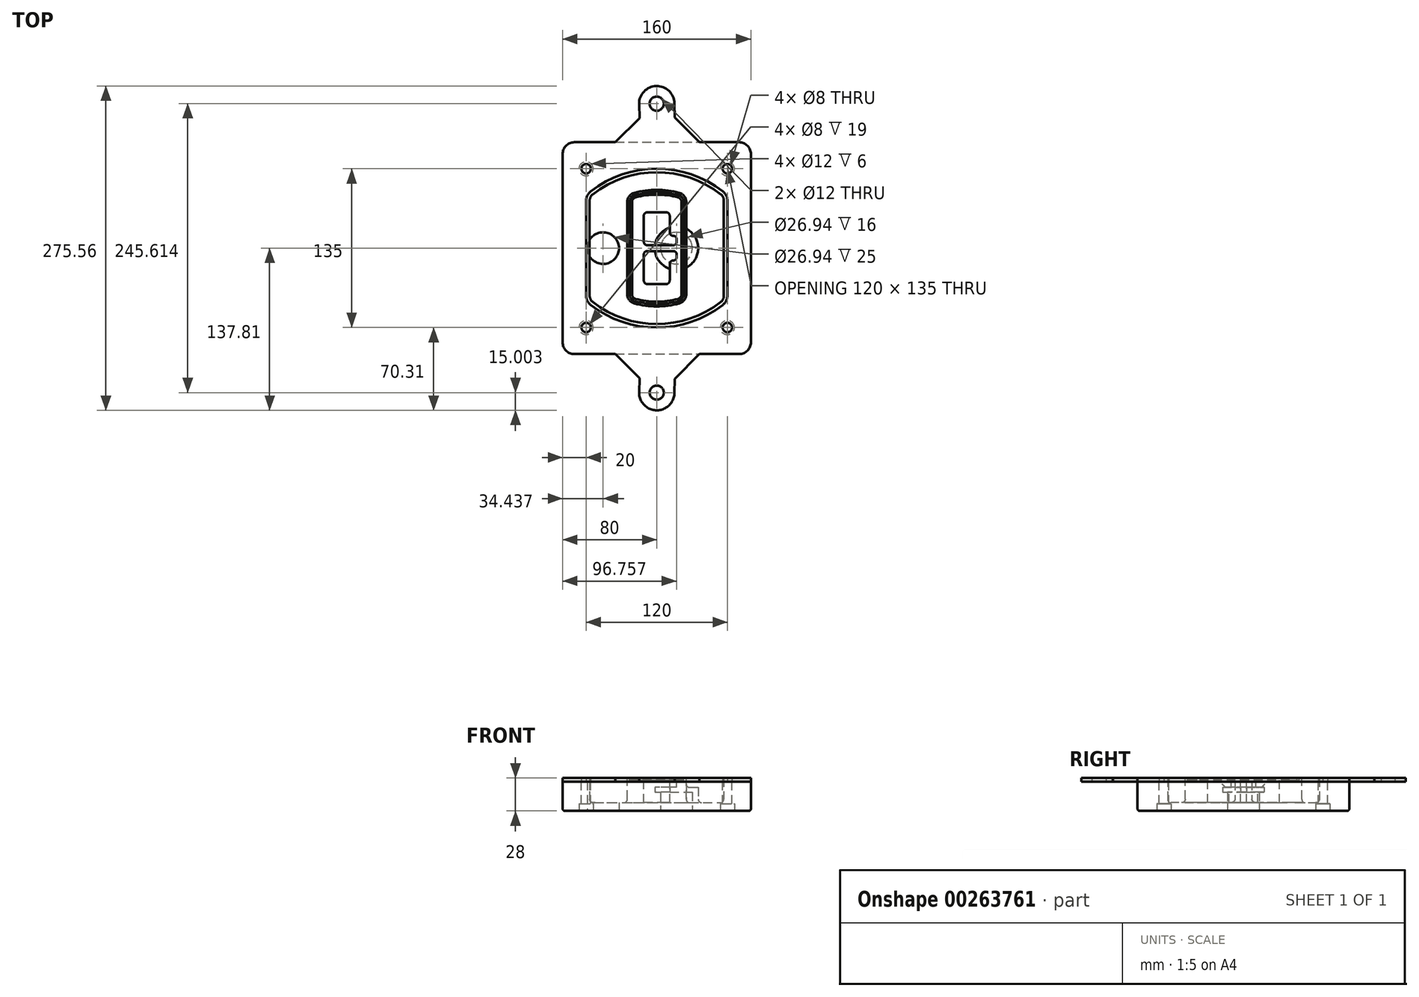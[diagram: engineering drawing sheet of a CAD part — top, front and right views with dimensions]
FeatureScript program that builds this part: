
annotation { "Feature Type Name" : "Feature", "Feature Type Description" : "" }
export const myFeature = defineFeature(function(context is Context, id is Id, definition is map)
    precondition{}
    {
        {
            var Q0;
            Q0=qCreatedBy(makeId("Top.planeOp"),FACE);
            var sketch = newSketch(context, id + "F0", { "sketchPlane" : qUnion([Q0])});
            skPoint(sketch, "E0.rect.middle", {"position": v(0, 0) * mm});
            skLineSegment(sketch, "E1.bottom", {"start": v(-70, -90) * mm, "end": v(70, -90) * mm});
            skLineSegment(sketch, "E1.top", {"start": v(-70, 90) * mm, "end": v(70, 90) * mm});
            skLineSegment(sketch, "E1.left", {"start": v(-80, -80) * mm, "end": v(-80, 80) * mm});
            skLineSegment(sketch, "E1.right", {"start": v(80, -80) * mm, "end": v(80, 80) * mm});
            skLineSegment(sketch, "E2", {"start": v(-80, 90) * mm, "end": v(80, -90) * mm, "construction": true});
            skLineSegment(sketch, "E3", {"start": v(80, 90) * mm, "end": v(-80, -90) * mm, "construction": true});
            skCircle(sketch, "E4", {"center": v(-60, 67.5) * mm, "radius": 4 * mm});
            skCircle(sketch, "E5", {"center": v(60, 67.5) * mm, "radius": 4 * mm});
            skCircle(sketch, "E6", {"center": v(60, -67.5) * mm, "radius": 4 * mm});
            skCircle(sketch, "E7", {"center": v(-60, -67.5) * mm, "radius": 4 * mm});
            skLineSegment(sketch, "E8", {"start": v(-60, 67.5) * mm, "end": v(60, 67.5) * mm, "construction": true});
            skLineSegment(sketch, "E9", {"start": v(60, 67.5) * mm, "end": v(60, -67.5) * mm, "construction": true});
            skLineSegment(sketch, "E10", {"start": v(60, -67.5) * mm, "end": v(-60, -67.5) * mm, "construction": true});
            skLineSegment(sketch, "E11", {"start": v(-60, -67.5) * mm, "end": v(-60, 67.5) * mm, "construction": true});
            skLineSegment(sketch, "E12", {"start": v(-60, 40.3) * mm, "end": v(-60, -40.3) * mm});
            skLineSegment(sketch, "E13", {"start": v(60, 40.3) * mm, "end": v(60, -40.3) * mm});
            skArc(sketch, "E14", {"start": v(56.15, 48.18) * mm, "mid": v(0, 67.5) * mm, "end": v(-56.15, 48.18) * mm});
            skArc(sketch, "E15", {"start": v(-56.15, -48.18) * mm, "mid": v(0, -67.5) * mm, "end": v(56.15, -48.18) * mm});
            skLineSegment(sketch, "E16", {"start": v(-60, 0) * mm, "end": v(60, 0) * mm, "construction": true});
            skPoint(sketch, "E17.visualSharp", {"position": v(-60, -45) * mm});
            skArc(sketch, "E17.filletArc", {"start": v(-60, -40.3) * mm, "mid": v(-58.99, -44.68) * mm, "end": v(-56.15, -48.18) * mm});
            skPoint(sketch, "E18.visualSharp", {"position": v(-60, 45) * mm});
            skArc(sketch, "E18.filletArc", {"start": v(-56.15, 48.18) * mm, "mid": v(-58.99, 44.68) * mm, "end": v(-60, 40.3) * mm});
            skPoint(sketch, "E19.visualSharp", {"position": v(60, 45) * mm});
            skArc(sketch, "E19.filletArc", {"start": v(60, 40.3) * mm, "mid": v(58.99, 44.68) * mm, "end": v(56.15, 48.18) * mm});
            skPoint(sketch, "E20.visualSharp", {"position": v(60, -45) * mm});
            skArc(sketch, "E20.filletArc", {"start": v(56.15, -48.18) * mm, "mid": v(58.99, -44.68) * mm, "end": v(60, -40.3) * mm});
            skPoint(sketch, "E21.visualSharp", {"position": v(-80, 90) * mm});
            skArc(sketch, "E21.filletArc", {"start": v(-70, 90) * mm, "mid": v(-77.07, 87.07) * mm, "end": v(-80, 80) * mm});
            skPoint(sketch, "E22.visualSharp", {"position": v(80, 90) * mm});
            skArc(sketch, "E22.filletArc", {"start": v(80, 80) * mm, "mid": v(77.07, 87.07) * mm, "end": v(70, 90) * mm});
            skPoint(sketch, "E23.visualSharp", {"position": v(80, -90) * mm});
            skArc(sketch, "E23.filletArc", {"start": v(70, -90) * mm, "mid": v(77.07, -87.07) * mm, "end": v(80, -80) * mm});
            skPoint(sketch, "E24.visualSharp", {"position": v(-80, -90) * mm});
            skArc(sketch, "E24.filletArc", {"start": v(-80, -80) * mm, "mid": v(-77.07, -87.07) * mm, "end": v(-70, -90) * mm});
            skArc(sketch, "E25.0", {"start": v(57, 40.3) * mm, "mid": v(56.3, 43.36) * mm, "end": v(54.3, 45.81) * mm});
            skLineSegment(sketch, "E25.1", {"start": v(57, 40.3) * mm, "end": v(57, -40.3) * mm});
            skArc(sketch, "E25.2", {"start": v(54.3, -45.81) * mm, "mid": v(56.3, -43.36) * mm, "end": v(57, -40.3) * mm});
            skArc(sketch, "E25.3", {"start": v(-54.3, -45.81) * mm, "mid": v(0, -64.5) * mm, "end": v(54.3, -45.81) * mm});
            skArc(sketch, "E25.4", {"start": v(-57, -40.3) * mm, "mid": v(-56.3, -43.36) * mm, "end": v(-54.3, -45.81) * mm});
            skArc(sketch, "E25.5", {"start": v(54.3, 45.81) * mm, "mid": v(0, 64.5) * mm, "end": v(-54.3, 45.81) * mm});
            skLineSegment(sketch, "E25.6", {"start": v(-57, 40.3) * mm, "end": v(-57, -40.3) * mm});
            skArc(sketch, "E25.7", {"start": v(-54.3, 45.81) * mm, "mid": v(-56.3, 43.36) * mm, "end": v(-57, 40.3) * mm});
            skArc(sketch, "E26.0", {"start": v(-58.62, 51.33) * mm, "mid": v(-62.58, 46.43) * mm, "end": v(-64, 40.3) * mm});
            skArc(sketch, "E26.1", {"start": v(58.62, 51.33) * mm, "mid": v(0, 71.5) * mm, "end": v(-58.62, 51.33) * mm});
            skArc(sketch, "E26.2", {"start": v(64, 40.3) * mm, "mid": v(62.58, 46.43) * mm, "end": v(58.62, 51.33) * mm});
            skLineSegment(sketch, "E26.3", {"start": v(64, 40.3) * mm, "end": v(64, -40.3) * mm});
            skArc(sketch, "E26.4", {"start": v(58.62, -51.33) * mm, "mid": v(62.58, -46.43) * mm, "end": v(64, -40.3) * mm});
            skLineSegment(sketch, "E26.5", {"start": v(-64, 40.3) * mm, "end": v(-64, -40.3) * mm});
            skArc(sketch, "E26.6", {"start": v(-58.62, -51.33) * mm, "mid": v(0, -71.5) * mm, "end": v(58.62, -51.33) * mm});
            skArc(sketch, "E26.7", {"start": v(-64, -40.3) * mm, "mid": v(-62.58, -46.43) * mm, "end": v(-58.62, -51.33) * mm});
            skSolve(sketch);
        }
        {
            var Q0;
            Q0=makeQuery(id+"F0.imprint","IMPRINT",FACE,{"disambiguationData":[TD([[makeQuery(id+"F0.imprint","IMPRINT",EDGE,{"derivedFrom":sQuery(id+"F0.wireOp",EDGE,"E1.bottom")}),1.0]])]});
            var Q1;
            Q1=makeQuery(id+"F0.imprint","IMPRINT",FACE,{"disambiguationData":[TD([[makeQuery(id+"F0.imprint","IMPRINT",EDGE,{"derivedFrom":sQuery(id+"F0.wireOp",EDGE,"E12")}),1.0]])]});
            var Q2;
            Q2=makeQuery(id+"F0.imprint","IMPRINT",FACE,{"disambiguationData":[TD([[makeQuery(id+"F0.imprint","IMPRINT",EDGE,{"derivedFrom":sQuery(id+"F0.wireOp",EDGE,"E25.0")}),1.0]])]});
            var Q3;
            Q3=makeQuery(id+"F0.imprint","IMPRINT",FACE,{"disambiguationData":[TD([[makeQuery(id+"F0.imprint","IMPRINT",EDGE,{"derivedFrom":sQuery(id+"F0.wireOp",EDGE,"E12")}),-1.0]])]});
            extrude(context, id + "F1", {"entities" : qUnion([Q0, Q1, Q2, Q3]), "oppositeDirection" : true, "depth" : 25 * mm});
        }
        {
            var Q0;
            Q0=makeQuery(id+"F0.imprint","IMPRINT",FACE,{"disambiguationData":[TD([[makeQuery(id+"F0.imprint","IMPRINT",EDGE,{"derivedFrom":sQuery(id+"F0.wireOp",EDGE,"E12")}),1.0]])]});
            extrude(context, id + "F2", {"entities" : qUnion([Q0]), "operationType" : NewBodyOperationType.ADD, "depth" : 3 * mm});
        }
        {
            var Q0;
            Q0=makeQuery(id+"F0.imprint","IMPRINT",FACE,{"disambiguationData":[TD([[makeQuery(id+"F0.imprint","IMPRINT",EDGE,{"derivedFrom":sQuery(id+"F0.wireOp",EDGE,"E25.0")}),1.0]])]});
            extrude(context, id + "F3", {"entities" : qUnion([Q0]), "operationType" : NewBodyOperationType.REMOVE, "oppositeDirection" : true, "depth" : 18 * mm});
        }
        {
            var Q0;
            Q0=makeQuery(id+"F2.opExtrude","CAP_FACE",FACE,{"disambiguationData":[OSD([sQuery(id+"F0.wireOp",EDGE,"E12"),sQuery(id+"F0.wireOp",EDGE,"E13"),sQuery(id+"F0.wireOp",EDGE,"E14"),sQuery(id+"F0.wireOp",EDGE,"E15"),sQuery(id+"F0.wireOp",EDGE,"E17.filletArc"),sQuery(id+"F0.wireOp",EDGE,"E18.filletArc"),sQuery(id+"F0.wireOp",EDGE,"E19.filletArc"),sQuery(id+"F0.wireOp",EDGE,"E20.filletArc"),sQuery(id+"F0.wireOp",EDGE,"E25.0"),sQuery(id+"F0.wireOp",EDGE,"E25.1"),sQuery(id+"F0.wireOp",EDGE,"E25.2"),sQuery(id+"F0.wireOp",EDGE,"E25.3"),sQuery(id+"F0.wireOp",EDGE,"E25.4"),sQuery(id+"F0.wireOp",EDGE,"E25.5"),sQuery(id+"F0.wireOp",EDGE,"E25.6"),sQuery(id+"F0.wireOp",EDGE,"E25.7")])],"isStart":false});
            var sketch = newSketch(context, id + "F4", { "sketchPlane" : qUnion([Q0])});
            skArc(sketch, "E27.0", {"start": v(-19.08, -46.97) * mm, "mid": v(0, -49.5) * mm, "end": v(19.08, -46.97) * mm});
            skArc(sketch, "E28.0", {"start": v(19.08, 46.97) * mm, "mid": v(0, 49.5) * mm, "end": v(-19.08, 46.97) * mm});
            skLineSegment(sketch, "E29", {"start": v(-25, 39.25) * mm, "end": v(-25, -39.25) * mm});
            skLineSegment(sketch, "E30", {"start": v(25, 39.25) * mm, "end": v(25, -39.25) * mm});
            skLineSegment(sketch, "E31", {"start": v(-25, 45.1) * mm, "end": v(25, 45.1) * mm, "construction": true});
            skLineSegment(sketch, "E32", {"start": v(-25, -45.1) * mm, "end": v(25, -45.1) * mm, "construction": true});
            skPoint(sketch, "E33.visualSharp", {"position": v(-25, 45.1) * mm});
            skArc(sketch, "E33.filletArc", {"start": v(-19.08, 46.97) * mm, "mid": v(-23.35, 44.11) * mm, "end": v(-25, 39.25) * mm});
            skPoint(sketch, "E34.visualSharp", {"position": v(25, 45.1) * mm});
            skArc(sketch, "E34.filletArc", {"start": v(25, 39.25) * mm, "mid": v(23.35, 44.11) * mm, "end": v(19.08, 46.97) * mm});
            skPoint(sketch, "E35.visualSharp", {"position": v(25, -45.1) * mm});
            skArc(sketch, "E35.filletArc", {"start": v(19.08, -46.97) * mm, "mid": v(23.35, -44.11) * mm, "end": v(25, -39.25) * mm});
            skPoint(sketch, "E36.visualSharp", {"position": v(-25, -45.1) * mm});
            skArc(sketch, "E36.filletArc", {"start": v(-25, -39.25) * mm, "mid": v(-23.35, -44.11) * mm, "end": v(-19.08, -46.97) * mm});
            skArc(sketch, "E37.0", {"start": v(54.3, 45.81) * mm, "mid": v(0, 64.5) * mm, "end": v(-54.3, 45.81) * mm});
            skArc(sketch, "E37.1", {"start": v(-54.3, 45.81) * mm, "mid": v(-56.3, 43.36) * mm, "end": v(-57, 40.3) * mm});
            skLineSegment(sketch, "E37.2", {"start": v(-57, 40.3) * mm, "end": v(-57, -40.3) * mm});
            skArc(sketch, "E37.3", {"start": v(-57, -40.3) * mm, "mid": v(-56.3, -43.36) * mm, "end": v(-54.3, -45.81) * mm});
            skArc(sketch, "E37.4", {"start": v(-54.3, -45.81) * mm, "mid": v(0, -64.5) * mm, "end": v(54.3, -45.81) * mm});
            skArc(sketch, "E37.5", {"start": v(54.3, -45.81) * mm, "mid": v(56.3, -43.36) * mm, "end": v(57, -40.3) * mm});
            skLineSegment(sketch, "E37.6", {"start": v(57, 40.3) * mm, "end": v(57, -40.3) * mm});
            skArc(sketch, "E37.7", {"start": v(57, 40.3) * mm, "mid": v(56.3, 43.36) * mm, "end": v(54.3, 45.81) * mm});
            skLineSegment(sketch, "E38.0", {"start": v(23, 39.25) * mm, "end": v(23, -39.25) * mm});
            skArc(sketch, "E38.1", {"start": v(18.56, -45.04) * mm, "mid": v(21.76, -42.9) * mm, "end": v(23, -39.25) * mm});
            skArc(sketch, "E38.2", {"start": v(-18.56, -45.04) * mm, "mid": v(0, -47.5) * mm, "end": v(18.56, -45.04) * mm});
            skArc(sketch, "E38.3", {"start": v(-23, -39.25) * mm, "mid": v(-21.76, -42.9) * mm, "end": v(-18.56, -45.04) * mm});
            skLineSegment(sketch, "E38.4", {"start": v(-23, 39.25) * mm, "end": v(-23, -39.25) * mm});
            skArc(sketch, "E38.5", {"start": v(23, 39.25) * mm, "mid": v(21.76, 42.9) * mm, "end": v(18.56, 45.04) * mm});
            skArc(sketch, "E38.6", {"start": v(-18.56, 45.04) * mm, "mid": v(-21.76, 42.9) * mm, "end": v(-23, 39.25) * mm});
            skArc(sketch, "E38.7", {"start": v(18.56, 45.04) * mm, "mid": v(0, 47.5) * mm, "end": v(-18.56, 45.04) * mm});
            skArc(sketch, "E39.0", {"start": v(21, 39.25) * mm, "mid": v(20.18, 41.68) * mm, "end": v(18.04, 43.1) * mm});
            skLineSegment(sketch, "E39.1", {"start": v(21, 39.25) * mm, "end": v(21, -39.25) * mm});
            skArc(sketch, "E39.2", {"start": v(18.04, -43.1) * mm, "mid": v(20.18, -41.68) * mm, "end": v(21, -39.25) * mm});
            skArc(sketch, "E39.3", {"start": v(-18.04, -43.1) * mm, "mid": v(0, -45.5) * mm, "end": v(18.04, -43.1) * mm});
            skArc(sketch, "E39.4", {"start": v(-21, -39.25) * mm, "mid": v(-20.18, -41.68) * mm, "end": v(-18.04, -43.1) * mm});
            skArc(sketch, "E39.5", {"start": v(18.04, 43.1) * mm, "mid": v(0, 45.5) * mm, "end": v(-18.04, 43.1) * mm});
            skLineSegment(sketch, "E39.6", {"start": v(-21, 39.25) * mm, "end": v(-21, -39.25) * mm});
            skArc(sketch, "E39.7", {"start": v(-18.04, 43.1) * mm, "mid": v(-20.18, 41.68) * mm, "end": v(-21, 39.25) * mm});
            skLineSegment(sketch, "E40", {"start": v(-25, 0) * mm, "end": v(25, 0) * mm, "construction": true});
            skLineSegment(sketch, "E41", {"start": v(-11, 5.5) * mm, "end": v(-11, 27.5) * mm});
            skLineSegment(sketch, "E42", {"start": v(-8, 30.5) * mm, "end": v(8, 30.5) * mm});
            skLineSegment(sketch, "E43", {"start": v(11, 27.5) * mm, "end": v(11, 13.5) * mm});
            skLineSegment(sketch, "E44", {"start": v(14, 10.5) * mm, "end": v(14, 10.5) * mm});
            skLineSegment(sketch, "E45", {"start": v(17, 7.5) * mm, "end": v(17, 5.5) * mm});
            skLineSegment(sketch, "E46", {"start": v(14, 2.5) * mm, "end": v(-8, 2.5) * mm});
            skPoint(sketch, "E47.visualSharp", {"position": v(-11, 30.5) * mm});
            skArc(sketch, "E47.filletArc", {"start": v(-8, 30.5) * mm, "mid": v(-10.12, 29.62) * mm, "end": v(-11, 27.5) * mm});
            skPoint(sketch, "E48.visualSharp", {"position": v(11, 30.5) * mm});
            skArc(sketch, "E48.filletArc", {"start": v(11, 27.5) * mm, "mid": v(10.12, 29.62) * mm, "end": v(8, 30.5) * mm});
            skPoint(sketch, "E49.visualSharp", {"position": v(11, 10.5) * mm});
            skArc(sketch, "E49.filletArc", {"start": v(11, 13.5) * mm, "mid": v(11.88, 11.38) * mm, "end": v(14, 10.5) * mm});
            skPoint(sketch, "E50.visualSharp", {"position": v(17, 10.5) * mm});
            skArc(sketch, "E50.filletArc", {"start": v(17, 7.5) * mm, "mid": v(16.12, 9.62) * mm, "end": v(14, 10.5) * mm});
            skPoint(sketch, "E51.visualSharp", {"position": v(17, 2.5) * mm});
            skArc(sketch, "E51.filletArc", {"start": v(14, 2.5) * mm, "mid": v(16.12, 3.38) * mm, "end": v(17, 5.5) * mm});
            skPoint(sketch, "E52.visualSharp", {"position": v(-11, 2.5) * mm});
            skArc(sketch, "E52.filletArc", {"start": v(-11, 5.5) * mm, "mid": v(-10.12, 3.38) * mm, "end": v(-8, 2.5) * mm});
            skLineSegment(sketch, "E53.0.MirrorCS", {"start": v(14, -2.5) * mm, "end": v(-8, -2.5) * mm});
            skArc(sketch, "E54.0.MirrorCS", {"start": v(-11, -5.5) * mm, "mid": v(-10.12, -3.38) * mm, "end": v(-8, -2.5) * mm});
            skLineSegment(sketch, "E55.0.MirrorCS", {"start": v(-11, -5.5) * mm, "end": v(-11, -27.5) * mm});
            skArc(sketch, "E56.0.MirrorCS", {"start": v(-8, -30.5) * mm, "mid": v(-10.12, -29.62) * mm, "end": v(-11, -27.5) * mm});
            skLineSegment(sketch, "E57.0.MirrorCS", {"start": v(-8, -30.5) * mm, "end": v(8, -30.5) * mm});
            skArc(sketch, "E58.0.MirrorCS", {"start": v(11, -27.5) * mm, "mid": v(10.12, -29.62) * mm, "end": v(8, -30.5) * mm});
            skLineSegment(sketch, "E59.0.MirrorCS", {"start": v(11, -27.5) * mm, "end": v(11, -13.5) * mm});
            skArc(sketch, "E60.0.MirrorCS", {"start": v(11, -13.5) * mm, "mid": v(11.88, -11.38) * mm, "end": v(14, -10.5) * mm});
            skArc(sketch, "E61.0.MirrorCS", {"start": v(17, -7.5) * mm, "mid": v(16.12, -9.62) * mm, "end": v(14, -10.5) * mm});
            skLineSegment(sketch, "E62.0.MirrorCS", {"start": v(17, -7.5) * mm, "end": v(17, -5.5) * mm});
            skArc(sketch, "E63.0.MirrorCS", {"start": v(14, -2.5) * mm, "mid": v(16.12, -3.38) * mm, "end": v(17, -5.5) * mm});
            skSolve(sketch);
        }
        {
            var Q0;
            Q0=makeQuery(id+"F4.imprint","IMPRINT",FACE,{"disambiguationData":[TD([[makeQuery(id+"F4.imprint","IMPRINT",EDGE,{"derivedFrom":sQuery(id+"F4.wireOp",EDGE,"E27.0")}),1.0]])]});
            var Q1;
            Q1=makeQuery(id+"F4.imprint","IMPRINT",FACE,{"disambiguationData":[TD([[makeQuery(id+"F4.imprint","IMPRINT",EDGE,{"derivedFrom":sQuery(id+"F4.wireOp",EDGE,"E38.0")}),-1.0]])]});
            var Q2;
            Q2=makeQuery(id+"F4.imprint","IMPRINT",FACE,{"disambiguationData":[TD([[makeQuery(id+"F4.imprint","IMPRINT",EDGE,{"derivedFrom":sQuery(id+"F4.wireOp",EDGE,"E39.0")}),1.0]])]});
            extrude(context, id + "F5", {"entities" : qUnion([Q0, Q1, Q2]), "operationType" : NewBodyOperationType.ADD, "endBound" : BoundingType.UP_TO_NEXT, "oppositeDirection" : true, "depth" : 25 * mm});
        }
        {
            var Q0;
            Q0=makeQuery(id+"F4.imprint","IMPRINT",FACE,{"disambiguationData":[TD([[makeQuery(id+"F4.imprint","IMPRINT",EDGE,{"derivedFrom":sQuery(id+"F4.wireOp",EDGE,"E38.0")}),-1.0]])]});
            extrude(context, id + "F6", {"entities" : qUnion([Q0]), "operationType" : NewBodyOperationType.REMOVE, "oppositeDirection" : true, "depth" : 2 * mm});
        }
        {
            var Q0;
            Q0=makeQuery(id+"F1.opExtrude","CAP_FACE",FACE,{"disambiguationData":[OSD([sQuery(id+"F0.wireOp",EDGE,"E1.bottom"),sQuery(id+"F0.wireOp",EDGE,"E1.top"),sQuery(id+"F0.wireOp",EDGE,"E1.left"),sQuery(id+"F0.wireOp",EDGE,"E1.right"),sQuery(id+"F0.wireOp",EDGE,"E4"),sQuery(id+"F0.wireOp",EDGE,"E5"),sQuery(id+"F0.wireOp",EDGE,"E6"),sQuery(id+"F0.wireOp",EDGE,"E7"),sQuery(id+"F0.wireOp",EDGE,"E21.filletArc"),sQuery(id+"F0.wireOp",EDGE,"E22.filletArc"),sQuery(id+"F0.wireOp",EDGE,"E23.filletArc"),sQuery(id+"F0.wireOp",EDGE,"E24.filletArc")])],"isStart":false});
            var sketch = newSketch(context, id + "F7", { "sketchPlane" : qUnion([Q0])});
            skCircle(sketch, "E64", {"center": v(16.76, 0) * mm, "radius": 13.47 * mm});
            skCircle(sketch, "E65", {"center": v(-45.56, 0) * mm, "radius": 13.47 * mm});
            skLineSegment(sketch, "E66", {"start": v(80, 0) * mm, "end": v(-80, 0) * mm});
            skCircle(sketch, "E67", {"center": v(16.76, 0) * mm, "radius": 18.47 * mm});
            skCircle(sketch, "E68", {"center": v(60, -67.5) * mm, "radius": 6 * mm});
            skCircle(sketch, "E69", {"center": v(-60, -67.5) * mm, "radius": 6 * mm});
            skCircle(sketch, "E70", {"center": v(-60, 67.5) * mm, "radius": 6 * mm});
            skCircle(sketch, "E71", {"center": v(60, 67.5) * mm, "radius": 6 * mm});
            skSolve(sketch);
        }
        {
            var Q0;
            {var subQ1=sQuery(id+"F7.wireOp",EDGE,"E66");var subQ4=sQuery(id+"F7.wireOp",EDGE,"E64");var subQ6=makeQuery(id+"F7.imprint","INTERSECT",VERTEX,{"disambiguationData":[OD(0.0)],"derivedFrom":[subQ4,subQ1]});Q0=makeQuery(id+"F7.imprint","IMPRINT",FACE,{"disambiguationData":[TD([[makeQuery(id+"F7.imprint","IMPRINT",EDGE,{"disambiguationData":[TD([[subQ6,-1.0]])],"derivedFrom":subQ4}),-1.0]])]});}
            var Q1;
            {var subQ0=sQuery(id+"F7.wireOp",EDGE,"E66");var subQ1=sQuery(id+"F7.wireOp",EDGE,"E64");var subQ3=makeQuery(id+"F7.imprint","INTERSECT",VERTEX,{"disambiguationData":[OD(0.0)],"derivedFrom":[subQ1,subQ0]});Q1=makeQuery(id+"F7.imprint","IMPRINT",FACE,{"disambiguationData":[TD([[makeQuery(id+"F7.imprint","IMPRINT",EDGE,{"disambiguationData":[TD([[subQ3,-1.0]])],"derivedFrom":subQ1}),1.0]])]});}
            var Q2;
            {var subQ0=sQuery(id+"F7.wireOp",EDGE,"E66");var subQ1=sQuery(id+"F7.wireOp",EDGE,"E64");var subQ3=makeQuery(id+"F7.imprint","INTERSECT",VERTEX,{"disambiguationData":[OD(0.0)],"derivedFrom":[subQ1,subQ0]});Q2=makeQuery(id+"F7.imprint","IMPRINT",FACE,{"disambiguationData":[TD([[makeQuery(id+"F7.imprint","IMPRINT",EDGE,{"disambiguationData":[TD([[subQ3,1.0]])],"derivedFrom":subQ1}),1.0]])]});}
            var Q3;
            {var subQ1=sQuery(id+"F7.wireOp",EDGE,"E66");var subQ4=sQuery(id+"F7.wireOp",EDGE,"E64");var subQ6=makeQuery(id+"F7.imprint","INTERSECT",VERTEX,{"disambiguationData":[OD(0.0)],"derivedFrom":[subQ4,subQ1]});Q3=makeQuery(id+"F7.imprint","IMPRINT",FACE,{"disambiguationData":[TD([[makeQuery(id+"F7.imprint","IMPRINT",EDGE,{"disambiguationData":[TD([[subQ6,1.0]])],"derivedFrom":subQ4}),-1.0]])]});}
            extrude(context, id + "F8", {"entities" : qUnion([Q0, Q1, Q2, Q3]), "operationType" : NewBodyOperationType.ADD, "oppositeDirection" : true, "depth" : 20 * mm});
        }
        {
            var Q0;
            {var subQ0=sQuery(id+"F7.wireOp",EDGE,"E66");var subQ1=sQuery(id+"F7.wireOp",EDGE,"E64");var subQ3=makeQuery(id+"F7.imprint","INTERSECT",VERTEX,{"disambiguationData":[OD(0.0)],"derivedFrom":[subQ1,subQ0]});Q0=makeQuery(id+"F7.imprint","IMPRINT",FACE,{"disambiguationData":[TD([[makeQuery(id+"F7.imprint","IMPRINT",EDGE,{"disambiguationData":[TD([[subQ3,-1.0]])],"derivedFrom":subQ1}),1.0]])]});}
            var Q1;
            {var subQ0=sQuery(id+"F7.wireOp",EDGE,"E66");var subQ1=sQuery(id+"F7.wireOp",EDGE,"E64");var subQ3=makeQuery(id+"F7.imprint","INTERSECT",VERTEX,{"disambiguationData":[OD(0.0)],"derivedFrom":[subQ1,subQ0]});Q1=makeQuery(id+"F7.imprint","IMPRINT",FACE,{"disambiguationData":[TD([[makeQuery(id+"F7.imprint","IMPRINT",EDGE,{"disambiguationData":[TD([[subQ3,1.0]])],"derivedFrom":subQ1}),1.0]])]});}
            extrude(context, id + "F9", {"entities" : qUnion([Q0, Q1]), "operationType" : NewBodyOperationType.REMOVE, "oppositeDirection" : true, "depth" : 16 * mm});
        }
        {
            var Q0;
            {var subQ0=sQuery(id+"F7.wireOp",EDGE,"E66");var subQ1=sQuery(id+"F7.wireOp",EDGE,"E65");var subQ3=makeQuery(id+"F7.imprint","INTERSECT",VERTEX,{"disambiguationData":[OD(0.0)],"derivedFrom":[subQ1,subQ0]});Q0=makeQuery(id+"F7.imprint","IMPRINT",FACE,{"disambiguationData":[TD([[makeQuery(id+"F7.imprint","IMPRINT",EDGE,{"disambiguationData":[TD([[subQ3,-1.0]])],"derivedFrom":subQ1}),1.0]])]});}
            var Q1;
            {var subQ0=sQuery(id+"F7.wireOp",EDGE,"E66");var subQ1=sQuery(id+"F7.wireOp",EDGE,"E65");var subQ3=makeQuery(id+"F7.imprint","INTERSECT",VERTEX,{"disambiguationData":[OD(0.0)],"derivedFrom":[subQ1,subQ0]});Q1=makeQuery(id+"F7.imprint","IMPRINT",FACE,{"disambiguationData":[TD([[makeQuery(id+"F7.imprint","IMPRINT",EDGE,{"disambiguationData":[TD([[subQ3,1.0]])],"derivedFrom":subQ1}),1.0]])]});}
            extrude(context, id + "F10", {"entities" : qUnion([Q0, Q1]), "operationType" : NewBodyOperationType.REMOVE, "oppositeDirection" : true, "depth" : 25 * mm});
        }
        {
            var Q0;
            Q0=makeQuery(id+"F7.imprint","IMPRINT",FACE,{"disambiguationData":[TD([[makeQuery(id+"F7.imprint","IMPRINT",EDGE,{"derivedFrom":sQuery(id+"F7.wireOp",EDGE,"E68")}),1.0]])]});
            var Q1;
            Q1=makeQuery(id+"F7.imprint","IMPRINT",FACE,{"disambiguationData":[TD([[makeQuery(id+"F7.imprint","IMPRINT",EDGE,{"derivedFrom":makeQuery(id+"F1.opExtrude","CAP_EDGE",EDGE,{"disambiguationData":[OSD([sQuery(id+"F0.wireOp",EDGE,"E5")])],"isStart":false})}),-1.0]])]});
            var Q2;
            Q2=makeQuery(id+"F7.imprint","IMPRINT",FACE,{"disambiguationData":[TD([[makeQuery(id+"F7.imprint","IMPRINT",EDGE,{"derivedFrom":sQuery(id+"F7.wireOp",EDGE,"E69")}),1.0]])]});
            var Q3;
            Q3=makeQuery(id+"F7.imprint","IMPRINT",FACE,{"disambiguationData":[TD([[makeQuery(id+"F7.imprint","IMPRINT",EDGE,{"derivedFrom":makeQuery(id+"F1.opExtrude","CAP_EDGE",EDGE,{"disambiguationData":[OSD([sQuery(id+"F0.wireOp",EDGE,"E4")])],"isStart":false})}),-1.0]])]});
            var Q4;
            Q4=makeQuery(id+"F7.imprint","IMPRINT",FACE,{"disambiguationData":[TD([[makeQuery(id+"F7.imprint","IMPRINT",EDGE,{"derivedFrom":sQuery(id+"F7.wireOp",EDGE,"E70")}),1.0]])]});
            var Q5;
            Q5=makeQuery(id+"F7.imprint","IMPRINT",FACE,{"disambiguationData":[TD([[makeQuery(id+"F7.imprint","IMPRINT",EDGE,{"derivedFrom":makeQuery(id+"F1.opExtrude","CAP_EDGE",EDGE,{"disambiguationData":[OSD([sQuery(id+"F0.wireOp",EDGE,"E7")])],"isStart":false})}),-1.0]])]});
            var Q6;
            Q6=makeQuery(id+"F7.imprint","IMPRINT",FACE,{"disambiguationData":[TD([[makeQuery(id+"F7.imprint","IMPRINT",EDGE,{"derivedFrom":sQuery(id+"F7.wireOp",EDGE,"E71")}),1.0]])]});
            var Q7;
            Q7=makeQuery(id+"F7.imprint","IMPRINT",FACE,{"disambiguationData":[TD([[makeQuery(id+"F7.imprint","IMPRINT",EDGE,{"derivedFrom":makeQuery(id+"F1.opExtrude","CAP_EDGE",EDGE,{"disambiguationData":[OSD([sQuery(id+"F0.wireOp",EDGE,"E6")])],"isStart":false})}),-1.0]])]});
            extrude(context, id + "F11", {"entities" : qUnion([Q0, Q1, Q2, Q3, Q4, Q5, Q6, Q7]), "operationType" : NewBodyOperationType.REMOVE, "oppositeDirection" : true, "depth" : 6 * mm});
        }
        {
            var Q0;
            Q0=makeQuery(id+"F9.boolean.opBoolean","COPY",FACE,{"derivedFrom":makeQuery(id+"F9.opExtrude","CAP_FACE",FACE,{"disambiguationData":[OSD([sQuery(id+"F7.wireOp",EDGE,"E64")])],"isStart":false})});
            var sketch = newSketch(context, id + "F12", { "sketchPlane" : qUnion([Q0])});
            skArc(sketch, "E72.0", {"start": v(11, 17.55) * mm, "mid": v(2.57, 11.82) * mm, "end": v(-1.54, 2.5) * mm});
            skArc(sketch, "E72.1", {"start": v(-1.54, -2.5) * mm, "mid": v(2.57, -11.82) * mm, "end": v(11, -17.55) * mm});
            skLineSegment(sketch, "E73", {"start": v(-1.54, -2.5) * mm, "end": v(14, -2.5) * mm});
            skLineSegment(sketch, "E74.0", {"start": v(14, 2.5) * mm, "end": v(-1.54, 2.5) * mm});
            skArc(sketch, "E74.1", {"start": v(14, 2.5) * mm, "mid": v(16.12, 3.38) * mm, "end": v(17, 5.5) * mm});
            skLineSegment(sketch, "E74.2", {"start": v(17, 7.5) * mm, "end": v(17, 5.5) * mm});
            skArc(sketch, "E74.3", {"start": v(17, 7.5) * mm, "mid": v(16.12, 9.62) * mm, "end": v(14, 10.5) * mm});
            skArc(sketch, "E74.4", {"start": v(11, 13.5) * mm, "mid": v(11.88, 11.38) * mm, "end": v(14, 10.5) * mm});
            skLineSegment(sketch, "E74.5", {"start": v(11, 17.55) * mm, "end": v(11, 13.5) * mm});
            skLineSegment(sketch, "E74.7", {"start": v(14, -2.5) * mm, "end": v(-1.54, -2.5) * mm});
            skArc(sketch, "E74.8", {"start": v(14, -2.5) * mm, "mid": v(16.12, -3.38) * mm, "end": v(17, -5.5) * mm});
            skLineSegment(sketch, "E74.9", {"start": v(17, -7.5) * mm, "end": v(17, -5.5) * mm});
            skArc(sketch, "E74.10", {"start": v(17, -7.5) * mm, "mid": v(16.12, -9.62) * mm, "end": v(14, -10.5) * mm});
            skArc(sketch, "E74.11", {"start": v(11, -13.5) * mm, "mid": v(11.88, -11.38) * mm, "end": v(14, -10.5) * mm});
            skLineSegment(sketch, "E74.12", {"start": v(11, -17.55) * mm, "end": v(11, -13.5) * mm});
            skPoint(sketch, "E75.orphan", {"position": v(11, -27.5) * mm});
            skPoint(sketch, "E76.orphan", {"position": v(-8, -2.5) * mm});
            skPoint(sketch, "E77.orphan", {"position": v(-8, 2.5) * mm});
            skPoint(sketch, "E78.orphan", {"position": v(11, 27.5) * mm});
            skSolve(sketch);
        }
        {
            var Q0;
            {var subQ7=sQuery(id+"F12.wireOp",EDGE,"E72.0");var subQ14=sQuery(id+"F12.wireOp",EDGE,"E72.1");var subQ16=sQuery(id+"F12.wireOp",EDGE,"E74.1");var subQ18=sQuery(id+"F12.wireOp",EDGE,"E74.8");Q0=qUnion([makeQuery(id+"F12.imprint","IMPRINT",FACE,{"disambiguationData":[TD([[makeQuery(id+"F12.imprint","IMPRINT",EDGE,{"derivedFrom":subQ7}),1.0]])]}),makeQuery(id+"F12.imprint","IMPRINT",FACE,{"disambiguationData":[TD([[makeQuery(id+"F12.imprint","IMPRINT",EDGE,{"derivedFrom":subQ14}),1.0]])]}),makeQuery(id+"F12.imprint","IMPRINT",FACE,{"disambiguationData":[TD([[makeQuery(id+"F12.imprint","IMPRINT",EDGE,{"derivedFrom":subQ16}),1.0]])]}),makeQuery(id+"F12.imprint","IMPRINT",FACE,{"disambiguationData":[TD([[makeQuery(id+"F12.imprint","IMPRINT",EDGE,{"derivedFrom":subQ18}),-1.0]])]})]);}
            var Q1;
            Q1=makeQuery(id+"F5.boolean.opBoolean","SPLIT",FACE,{"disambiguationData":[TD([makeQuery(id+"F5.opExtrude","SWEPT_FACE",FACE,{"disambiguationData":[OSD([sQuery(id+"F4.wireOp",EDGE,"E41")])]})])],"derivedFrom":makeQuery(id+"F3.boolean.opBoolean","COPY",FACE,{"derivedFrom":makeQuery(id+"F3.opExtrude","CAP_FACE",FACE,{"disambiguationData":[OSD([sQuery(id+"F0.wireOp",EDGE,"E25.0"),sQuery(id+"F0.wireOp",EDGE,"E25.1"),sQuery(id+"F0.wireOp",EDGE,"E25.2"),sQuery(id+"F0.wireOp",EDGE,"E25.3"),sQuery(id+"F0.wireOp",EDGE,"E25.4"),sQuery(id+"F0.wireOp",EDGE,"E25.5"),sQuery(id+"F0.wireOp",EDGE,"E25.6"),sQuery(id+"F0.wireOp",EDGE,"E25.7")])],"isStart":false})})});
            extrude(context, id + "F13", {"entities" : qUnion([Q0]), "operationType" : NewBodyOperationType.REMOVE, "endBound" : BoundingType.UP_TO_SURFACE, "endBoundEntityFace" : qUnion([Q1]), "depth" : 25 * mm});
        }
        {
            var Q0;
            Q0=makeQuery(id+"F3.boolean.opBoolean","COPY",EDGE,{"derivedFrom":makeQuery(id+"F3.opExtrude","CAP_EDGE",EDGE,{"disambiguationData":[OSD([sQuery(id+"F0.wireOp",EDGE,"E25.6")])],"isStart":false})});
            var Q1;
            Q1=makeQuery(id+"F8.boolean.opBoolean","INTERSECT",EDGE,{"derivedFrom":[makeQuery(id+"F5.opExtrude","SWEPT_FACE",FACE,{"disambiguationData":[OSD([sQuery(id+"F4.wireOp",EDGE,"E30")])]}),makeQuery(id+"F8.opExtrude","CAP_FACE",FACE,{"disambiguationData":[OSD([sQuery(id+"F7.wireOp",EDGE,"E67")])],"isStart":false})]});
            var Q2;
            Q2=makeQuery(id+"F8.boolean.opBoolean","INTERSECT",EDGE,{"disambiguationData":[OD(1.0)],"derivedFrom":[makeQuery(id+"F5.opExtrude","SWEPT_FACE",FACE,{"disambiguationData":[OSD([sQuery(id+"F4.wireOp",EDGE,"E30")])]}),makeQuery(id+"F8.opExtrude","SWEPT_FACE",FACE,{"disambiguationData":[OSD([sQuery(id+"F7.wireOp",EDGE,"E67")])]})]});
            var Q3;
            {var subQ0=sQuery(id+"F4.wireOp",EDGE,"E30");Q3=makeQuery(id+"F8.boolean.opBoolean","SPLIT",EDGE,{"disambiguationData":[TD([makeQuery(id+"F5.opExtrude","SWEPT_FACE",FACE,{"disambiguationData":[OSD([sQuery(id+"F4.wireOp",EDGE,"E35.filletArc")])]})])],"derivedFrom":makeQuery(id+"F5.opExtrude","CAP_EDGE",EDGE,{"disambiguationData":[OSD([subQ0])],"isStart":false})});}
            var Q4;
            {var subQ0=sQuery(id+"F0.wireOp",EDGE,"E25.7");var subQ1=sQuery(id+"F0.wireOp",EDGE,"E25.1");var subQ2=sQuery(id+"F0.wireOp",EDGE,"E25.6");var subQ3=sQuery(id+"F0.wireOp",EDGE,"E25.5");var subQ4=sQuery(id+"F0.wireOp",EDGE,"E25.4");var subQ5=sQuery(id+"F0.wireOp",EDGE,"E25.0");var subQ6=sQuery(id+"F0.wireOp",EDGE,"E25.2");var subQ7=sQuery(id+"F0.wireOp",EDGE,"E25.3");Q4=makeQuery(id+"F8.boolean.opBoolean","INTERSECT",EDGE,{"derivedFrom":[makeQuery(id+"F5.boolean.opBoolean","SPLIT",FACE,{"disambiguationData":[TD([makeQuery(id+"F2.opExtrude","SWEPT_FACE",FACE,{"disambiguationData":[OSD([subQ5])]})])],"derivedFrom":makeQuery(id+"F3.boolean.opBoolean","COPY",FACE,{"derivedFrom":makeQuery(id+"F3.opExtrude","CAP_FACE",FACE,{"disambiguationData":[OSD([subQ5,subQ1,subQ6,subQ7,subQ4,subQ3,subQ2,subQ0])],"isStart":false})})}),makeQuery(id+"F8.opExtrude","SWEPT_FACE",FACE,{"disambiguationData":[OSD([sQuery(id+"F7.wireOp",EDGE,"E67")])]})]});}
            var Q5;
            Q5=makeQuery(id+"F8.boolean.opBoolean","INTERSECT",EDGE,{"disambiguationData":[OD(0.0)],"derivedFrom":[makeQuery(id+"F5.opExtrude","SWEPT_FACE",FACE,{"disambiguationData":[OSD([sQuery(id+"F4.wireOp",EDGE,"E30")])]}),makeQuery(id+"F8.opExtrude","SWEPT_FACE",FACE,{"disambiguationData":[OSD([sQuery(id+"F7.wireOp",EDGE,"E67")])]})]});
            fillet(context, id + "F14", {"entities" : qUnion([Q0, Q1, Q2, Q3, Q4, Q5]), "radius" : 3 * mm, "tangentPropagation" : true, "allowEdgeOverflow" : false});
        }
        {
            var Q0;
            Q0=makeQuery(id+"F1.opExtrude","CAP_EDGE",EDGE,{"disambiguationData":[OSD([sQuery(id+"F0.wireOp",EDGE,"E1.bottom")])],"isStart":false});
            fillet(context, id + "F15", {"entities" : qUnion([Q0]), "radius" : 2 * mm, "tangentPropagation" : true, "allowEdgeOverflow" : false});
        }
        {
            var Q0;
            {var subQ0=sQuery(id+"F0.wireOp",EDGE,"E22.filletArc");var subQ1=sQuery(id+"F0.wireOp",EDGE,"E7");var subQ2=sQuery(id+"F0.wireOp",EDGE,"E6");var subQ3=sQuery(id+"F0.wireOp",EDGE,"E5");var subQ4=sQuery(id+"F0.wireOp",EDGE,"E4");var subQ5=sQuery(id+"F0.wireOp",EDGE,"E1.bottom");var subQ6=sQuery(id+"F0.wireOp",EDGE,"E21.filletArc");var subQ7=sQuery(id+"F0.wireOp",EDGE,"E1.top");var subQ8=sQuery(id+"F0.wireOp",EDGE,"E1.left");var subQ9=sQuery(id+"F0.wireOp",EDGE,"E1.right");var subQ10=sQuery(id+"F0.wireOp",EDGE,"E23.filletArc");var subQ11=sQuery(id+"F0.wireOp",EDGE,"E24.filletArc");Q0=makeQuery(id+"F2.boolean.opBoolean","SPLIT",FACE,{"disambiguationData":[TD([makeQuery(id+"F1.opExtrude","SWEPT_FACE",FACE,{"disambiguationData":[OSD([subQ5])]})])],"derivedFrom":makeQuery(id+"F1.opExtrude","CAP_FACE",FACE,{"disambiguationData":[OSD([subQ5,subQ7,subQ8,subQ9,subQ4,subQ3,subQ2,subQ1,subQ6,subQ0,subQ10,subQ11])],"isStart":true})});}
            var sketch = newSketch(context, id + "F16", { "sketchPlane" : qUnion([Q0])});
            skLineSegment(sketch, "E79", {"start": v(0, 77.06) * mm, "end": v(0, 90) * mm});
            skPoint(sketch, "E79.endSnap0", {"position": v(0, 90) * mm});
            skCircle(sketch, "E80", {"center": v(0, 122.8) * mm, "radius": 6 * mm});
            skLineSegment(sketch, "E81", {"start": v(-15, 122.45) * mm, "end": v(-14.7, 110.45) * mm});
            skLineSegment(sketch, "E82", {"start": v(15, 123.11) * mm, "end": v(15.24, 111.11) * mm});
            skLineSegment(sketch, "E83", {"start": v(-14.7, 110.45) * mm, "end": v(-35.16, 90) * mm});
            skLineSegment(sketch, "E84", {"start": v(15.24, 111.11) * mm, "end": v(36.35, 90) * mm});
            skLineSegment(sketch, "E85", {"start": v(-80, 0) * mm, "end": v(80, 0) * mm});
            skLineSegment(sketch, "E86.MirrorCS", {"start": v(0, -77.06) * mm, "end": v(0, -90) * mm});
            skLineSegment(sketch, "E87.MirrorCS", {"start": v(15, -123.11) * mm, "end": v(15.24, -111.11) * mm});
            skLineSegment(sketch, "E88.MirrorCS", {"start": v(-15, -122.45) * mm, "end": v(-14.7, -110.45) * mm});
            skLineSegment(sketch, "E89.MirrorCS", {"start": v(15.24, -111.11) * mm, "end": v(36.35, -90) * mm});
            skLineSegment(sketch, "E90.MirrorCS", {"start": v(-14.7, -110.45) * mm, "end": v(-35.16, -90) * mm});
            skArc(sketch, "E91.MirrorC", {"start": v(15, -123.11) * mm, "mid": v(-0.33, -137.8) * mm, "end": v(-15, -122.45) * mm});
            skCircle(sketch, "E92.MirrorC", {"center": v(0, -122.8) * mm, "radius": 6 * mm});
            skPoint(sketch, "E93.MirrorP", {"position": v(0, -90) * mm});
            skLineSegment(sketch, "E94", {"start": v(-35.16, -90) * mm, "end": v(36.35, -90) * mm});
            skLineSegment(sketch, "E95", {"start": v(-35.16, 90) * mm, "end": v(36.35, 90) * mm});
            skArc(sketch, "E96", {"start": v(15, 123.11) * mm, "mid": v(-0.33, 137.75) * mm, "end": v(-15, 122.45) * mm});
            skSolve(sketch);
        }
        {
            var Q0;
            Q0 = qSketchRegion(id + "F16", true);
            var Q1;
            Q1=makeQuery(id+"F16.imprint","IMPRINT",FACE,{"disambiguationData":[TD([[makeQuery(id+"F16.imprint","IMPRINT",EDGE,{"derivedFrom":makeQuery(id+"F1.opExtrude","CAP_EDGE",EDGE,{"disambiguationData":[OSD([sQuery(id+"F0.wireOp",EDGE,"E4")])],"isStart":true})}),-1.0]])]});
            var Q2;
            Q2=makeQuery(id+"F16.imprint","IMPRINT",FACE,{"disambiguationData":[TD([[makeQuery(id+"F16.imprint","IMPRINT",EDGE,{"derivedFrom":makeQuery(id+"F1.opExtrude","CAP_EDGE",EDGE,{"disambiguationData":[OSD([sQuery(id+"F0.wireOp",EDGE,"E6")])],"isStart":true})}),-1.0]])]});
            var Q3;
            Q3=makeQuery(id+"F2.opExtrude","CAP_FACE",FACE,{"disambiguationData":[OSD([sQuery(id+"F0.wireOp",EDGE,"E12"),sQuery(id+"F0.wireOp",EDGE,"E13"),sQuery(id+"F0.wireOp",EDGE,"E14"),sQuery(id+"F0.wireOp",EDGE,"E15"),sQuery(id+"F0.wireOp",EDGE,"E17.filletArc"),sQuery(id+"F0.wireOp",EDGE,"E18.filletArc"),sQuery(id+"F0.wireOp",EDGE,"E19.filletArc"),sQuery(id+"F0.wireOp",EDGE,"E20.filletArc"),sQuery(id+"F0.wireOp",EDGE,"E25.0"),sQuery(id+"F0.wireOp",EDGE,"E25.1"),sQuery(id+"F0.wireOp",EDGE,"E25.2"),sQuery(id+"F0.wireOp",EDGE,"E25.3"),sQuery(id+"F0.wireOp",EDGE,"E25.4"),sQuery(id+"F0.wireOp",EDGE,"E25.5"),sQuery(id+"F0.wireOp",EDGE,"E25.6"),sQuery(id+"F0.wireOp",EDGE,"E25.7")])],"isStart":false});
            extrude(context, id + "F17", {"entities" : qUnion([Q0, Q1, Q2]), "endBound" : BoundingType.UP_TO_SURFACE, "endBoundEntityFace" : qUnion([Q3]), "depth" : 25 * mm});
        }
    });
